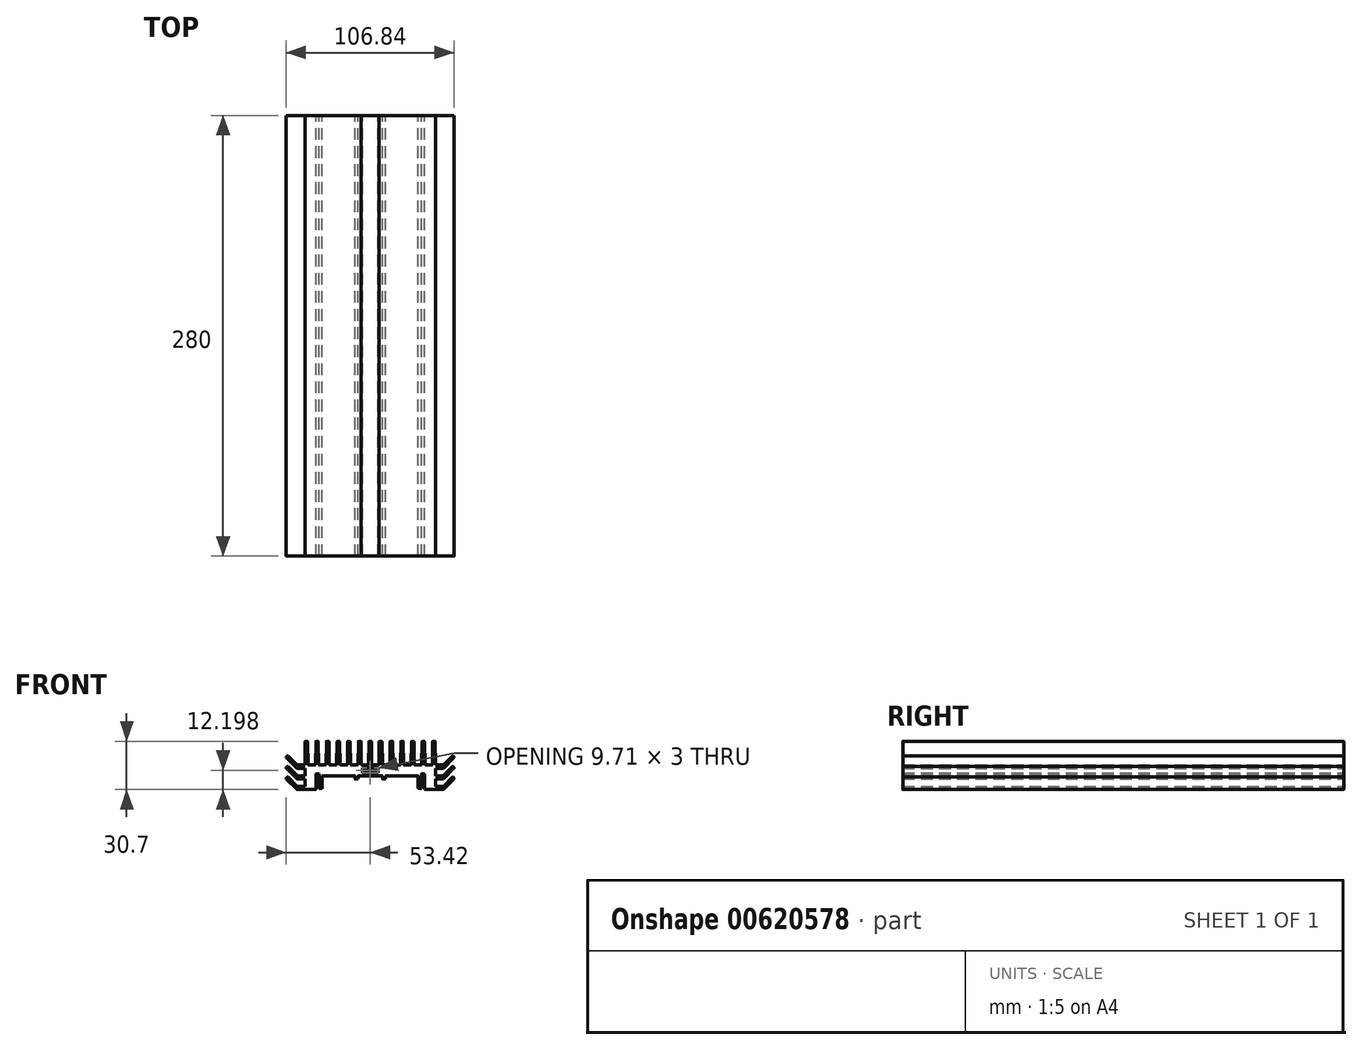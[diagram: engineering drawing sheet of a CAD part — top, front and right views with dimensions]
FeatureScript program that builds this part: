
annotation { "Feature Type Name" : "Feature", "Feature Type Description" : "" }
export const myFeature = defineFeature(function(context is Context, id is Id, definition is map)
    precondition{}
    {
        {
            var Q0;
            Q0=qCreatedBy(makeId("Front.planeOp"),FACE);
            var sketch = newSketch(context, id + "F0", { "sketchPlane" : qUnion([Q0])});
            skLineSegment(sketch, "E0", {"start": v(-32.5, -11.3) * mm, "end": v(-32.5, -2.4) * mm});
            skLineSegment(sketch, "E1", {"start": v(-32.7, -2.2) * mm, "end": v(-34.3, -2.2) * mm});
            skLineSegment(sketch, "E2", {"start": v(-34.5, -2.4) * mm, "end": v(-34.5, -12) * mm});
            skLineSegment(sketch, "E3", {"start": v(-39.75, 18.3) * mm, "end": v(-39.5, 3.7) * mm});
            skLineSegment(sketch, "E4", {"start": v(-9.75, -3.7) * mm, "end": v(-9.75, -5.3) * mm});
            skLineSegment(sketch, "E5", {"start": v(-9.55, -5.5) * mm, "end": v(-7.95, -5.5) * mm});
            skLineSegment(sketch, "E6", {"start": v(-39.3, 3.5) * mm, "end": v(-34.95, 3.5) * mm});
            skLineSegment(sketch, "E7", {"start": v(-41.5, 3.5) * mm, "end": v(-41.25, 18.3) * mm});
            skLineSegment(sketch, "E8", {"start": v(-41.05, 18.5) * mm, "end": v(-39.95, 18.5) * mm});
            skLineSegment(sketch, "E9", {"start": v(-41.5, 3.5) * mm, "end": v(-41.5, -12.2) * mm});
            skLineSegment(sketch, "E10.1.0.0", {"start": v(-33, 18.3) * mm, "end": v(-32.75, 3.7) * mm});
            skLineSegment(sketch, "E10.1.0.1", {"start": v(-32.55, 3.5) * mm, "end": v(-28.2, 3.5) * mm});
            skLineSegment(sketch, "E10.1.0.2", {"start": v(-34.75, 3.7) * mm, "end": v(-34.5, 18.3) * mm});
            skLineSegment(sketch, "E10.1.0.3", {"start": v(-34.3, 18.5) * mm, "end": v(-33.2, 18.5) * mm});
            skLineSegment(sketch, "E10.2.0.0", {"start": v(-26.25, 18.3) * mm, "end": v(-26, 3.7) * mm});
            skLineSegment(sketch, "E10.2.0.1", {"start": v(-25.8, 3.5) * mm, "end": v(-21.45, 3.5) * mm});
            skLineSegment(sketch, "E10.2.0.2", {"start": v(-28, 3.7) * mm, "end": v(-27.75, 18.3) * mm});
            skLineSegment(sketch, "E10.2.0.3", {"start": v(-27.55, 18.5) * mm, "end": v(-26.45, 18.5) * mm});
            skLineSegment(sketch, "E10.3.0.0", {"start": v(-19.5, 18.3) * mm, "end": v(-19.25, 3.7) * mm});
            skLineSegment(sketch, "E10.3.0.1", {"start": v(-19.05, 3.5) * mm, "end": v(-14.7, 3.5) * mm});
            skLineSegment(sketch, "E10.3.0.2", {"start": v(-21.25, 3.7) * mm, "end": v(-21, 18.3) * mm});
            skLineSegment(sketch, "E10.3.0.3", {"start": v(-20.8, 18.5) * mm, "end": v(-19.7, 18.5) * mm});
            skLineSegment(sketch, "E10.4.0.0", {"start": v(-12.75, 18.3) * mm, "end": v(-12.5, 3.7) * mm});
            skLineSegment(sketch, "E10.4.0.1", {"start": v(-12.3, 3.5) * mm, "end": v(-7.95, 3.5) * mm});
            skLineSegment(sketch, "E10.4.0.2", {"start": v(-14.5, 3.7) * mm, "end": v(-14.25, 18.3) * mm});
            skLineSegment(sketch, "E10.4.0.3", {"start": v(-14.05, 18.5) * mm, "end": v(-12.95, 18.5) * mm});
            skLineSegment(sketch, "E10.5.0.0", {"start": v(-5.75, 18.3) * mm, "end": v(-5.75, 3.7) * mm});
            skLineSegment(sketch, "E10.5.0.1", {"start": v(-5.55, 3.5) * mm, "end": v(-1.2, 3.5) * mm});
            skLineSegment(sketch, "E10.5.0.2", {"start": v(-7.75, 3.7) * mm, "end": v(-7.5, 18.3) * mm});
            skLineSegment(sketch, "E10.5.0.3", {"start": v(-7.3, 18.5) * mm, "end": v(-5.95, 18.5) * mm});
            skLineSegment(sketch, "E11.6.6.0", {"start": v(-1, 3.7) * mm, "end": v(-0.75, 18.3) * mm});
            skLineSegment(sketch, "E11.9.6.0", {"start": v(-0.55, 18.5) * mm, "end": v(0, 18.5) * mm});
            skPoint(sketch, "E12", {"position": v(0, 18.5) * mm});
            skLineSegment(sketch, "E13", {"start": v(0, 18.5) * mm, "end": v(0, 1.5) * mm});
            skLineSegment(sketch, "E14", {"start": v(-41.5, -12.2) * mm, "end": v(-34.7, -12.2) * mm});
            skLineSegment(sketch, "E15", {"start": v(-32.3, -11.5) * mm, "end": v(-30.7, -11.5) * mm});
            skLineSegment(sketch, "E16", {"start": v(-9.95, -3.5) * mm, "end": v(-30.32, -3.5) * mm});
            skLineSegment(sketch, "E17", {"start": v(-30.5, -11.3) * mm, "end": v(-30.52, -3.7) * mm});
            skLineSegment(sketch, "E18", {"start": v(-4.85, 1.3) * mm, "end": v(-4.85, -1.3) * mm});
            skLineSegment(sketch, "E19", {"start": v(0, -1.5) * mm, "end": v(0, -3.5) * mm});
            skLineSegment(sketch, "E20", {"start": v(-7.75, -3.7) * mm, "end": v(-7.75, -5.3) * mm});
            skPoint(sketch, "E21.visualSharp", {"position": v(-41.25, 18.5) * mm});
            skArc(sketch, "E21.filletArc", {"start": v(-41.05, 18.5) * mm, "mid": v(-41.2, 18.44) * mm, "end": v(-41.25, 18.3) * mm});
            skPoint(sketch, "E22.visualSharp", {"position": v(-39.75, 18.5) * mm});
            skArc(sketch, "E22.filletArc", {"start": v(-39.75, 18.3) * mm, "mid": v(-39.8, 18.44) * mm, "end": v(-39.95, 18.5) * mm});
            skPoint(sketch, "E23.visualSharp", {"position": v(-34.5, 18.5) * mm});
            skArc(sketch, "E23.filletArc", {"start": v(-34.3, 18.5) * mm, "mid": v(-34.44, 18.44) * mm, "end": v(-34.5, 18.3) * mm});
            skPoint(sketch, "E24.visualSharp", {"position": v(-33, 18.5) * mm});
            skArc(sketch, "E24.filletArc", {"start": v(-33, 18.3) * mm, "mid": v(-33.06, 18.44) * mm, "end": v(-33.2, 18.5) * mm});
            skPoint(sketch, "E25.visualSharp", {"position": v(-27.75, 18.5) * mm});
            skArc(sketch, "E25.filletArc", {"start": v(-27.55, 18.5) * mm, "mid": v(-27.7, 18.44) * mm, "end": v(-27.75, 18.3) * mm});
            skPoint(sketch, "E26.visualSharp", {"position": v(-26.25, 18.5) * mm});
            skArc(sketch, "E26.filletArc", {"start": v(-26.25, 18.3) * mm, "mid": v(-26.3, 18.44) * mm, "end": v(-26.45, 18.5) * mm});
            skPoint(sketch, "E27.visualSharp", {"position": v(-21, 18.5) * mm});
            skArc(sketch, "E27.filletArc", {"start": v(-20.8, 18.5) * mm, "mid": v(-20.94, 18.44) * mm, "end": v(-21, 18.3) * mm});
            skPoint(sketch, "E28.visualSharp", {"position": v(-19.5, 18.5) * mm});
            skArc(sketch, "E28.filletArc", {"start": v(-19.5, 18.3) * mm, "mid": v(-19.56, 18.44) * mm, "end": v(-19.7, 18.5) * mm});
            skPoint(sketch, "E29.visualSharp", {"position": v(-14.25, 18.5) * mm});
            skArc(sketch, "E29.filletArc", {"start": v(-14.05, 18.5) * mm, "mid": v(-14.2, 18.44) * mm, "end": v(-14.25, 18.3) * mm});
            skPoint(sketch, "E30.visualSharp", {"position": v(-12.75, 18.5) * mm});
            skArc(sketch, "E30.filletArc", {"start": v(-12.75, 18.3) * mm, "mid": v(-12.8, 18.44) * mm, "end": v(-12.95, 18.5) * mm});
            skPoint(sketch, "E31.visualSharp", {"position": v(-7.5, 18.5) * mm});
            skArc(sketch, "E31.filletArc", {"start": v(-7.3, 18.5) * mm, "mid": v(-7.44, 18.44) * mm, "end": v(-7.5, 18.3) * mm});
            skPoint(sketch, "E32.visualSharp", {"position": v(-5.75, 18.5) * mm});
            skArc(sketch, "E32.filletArc", {"start": v(-5.75, 18.3) * mm, "mid": v(-5.8, 18.44) * mm, "end": v(-5.95, 18.5) * mm});
            skPoint(sketch, "E33.visualSharp", {"position": v(-0.75, 18.5) * mm});
            skArc(sketch, "E33.filletArc", {"start": v(-0.55, 18.5) * mm, "mid": v(-0.7, 18.44) * mm, "end": v(-0.75, 18.3) * mm});
            skPoint(sketch, "E34.visualSharp", {"position": v(0, 1.5) * mm});
            skPoint(sketch, "E35.visualSharp", {"position": v(-4.85, 1.5) * mm});
            skArc(sketch, "E35.filletArc", {"start": v(-4.65, 1.5) * mm, "mid": v(-4.8, 1.44) * mm, "end": v(-4.85, 1.3) * mm});
            skPoint(sketch, "E36.visualSharp", {"position": v(-4.85, -1.5) * mm});
            skArc(sketch, "E36.filletArc", {"start": v(-4.85, -1.3) * mm, "mid": v(-4.8, -1.44) * mm, "end": v(-4.65, -1.5) * mm});
            skPoint(sketch, "E37.visualSharp", {"position": v(0, -1.5) * mm});
            skPoint(sketch, "E38.visualSharp", {"position": v(0, -3.5) * mm});
            skPoint(sketch, "E39.visualSharp", {"position": v(-7.75, -3.5) * mm});
            skArc(sketch, "E39.filletArc", {"start": v(-7.55, -3.5) * mm, "mid": v(-7.7, -3.56) * mm, "end": v(-7.75, -3.7) * mm});
            skPoint(sketch, "E40.visualSharp", {"position": v(-7.75, -5.5) * mm});
            skArc(sketch, "E40.filletArc", {"start": v(-7.95, -5.5) * mm, "mid": v(-7.8, -5.44) * mm, "end": v(-7.75, -5.3) * mm});
            skPoint(sketch, "E41.visualSharp", {"position": v(-9.75, -5.5) * mm});
            skArc(sketch, "E41.filletArc", {"start": v(-9.75, -5.3) * mm, "mid": v(-9.7, -5.44) * mm, "end": v(-9.55, -5.5) * mm});
            skPoint(sketch, "E42.visualSharp", {"position": v(-9.75, -3.5) * mm});
            skArc(sketch, "E42.filletArc", {"start": v(-9.75, -3.7) * mm, "mid": v(-9.8, -3.56) * mm, "end": v(-9.95, -3.5) * mm});
            skPoint(sketch, "E43.visualSharp", {"position": v(-30.52, -3.5) * mm});
            skArc(sketch, "E43.filletArc", {"start": v(-30.32, -3.5) * mm, "mid": v(-30.46, -3.56) * mm, "end": v(-30.52, -3.7) * mm});
            skPoint(sketch, "E44.visualSharp", {"position": v(-30.5, -11.5) * mm});
            skArc(sketch, "E44.filletArc", {"start": v(-30.7, -11.5) * mm, "mid": v(-30.56, -11.44) * mm, "end": v(-30.5, -11.3) * mm});
            skPoint(sketch, "E45.visualSharp", {"position": v(-32.5, -11.5) * mm});
            skArc(sketch, "E45.filletArc", {"start": v(-32.5, -11.3) * mm, "mid": v(-32.44, -11.44) * mm, "end": v(-32.3, -11.5) * mm});
            skPoint(sketch, "E46.visualSharp", {"position": v(-32.5, -2.2) * mm});
            skArc(sketch, "E46.filletArc", {"start": v(-32.5, -2.4) * mm, "mid": v(-32.56, -2.25) * mm, "end": v(-32.7, -2.2) * mm});
            skPoint(sketch, "E47.visualSharp", {"position": v(-34.5, -2.2) * mm});
            skArc(sketch, "E47.filletArc", {"start": v(-34.3, -2.2) * mm, "mid": v(-34.44, -2.25) * mm, "end": v(-34.5, -2.4) * mm});
            skPoint(sketch, "E48.visualSharp", {"position": v(-34.5, -12.2) * mm});
            skArc(sketch, "E48.filletArc", {"start": v(-34.7, -12.2) * mm, "mid": v(-34.56, -12.14) * mm, "end": v(-34.5, -12) * mm});
            skPoint(sketch, "E49.visualSharp", {"position": v(-41.5, -12.2) * mm});
            skPoint(sketch, "E50.visualSharp", {"position": v(-39.5, 3.5) * mm});
            skArc(sketch, "E50.filletArc", {"start": v(-39.5, 3.7) * mm, "mid": v(-39.44, 3.56) * mm, "end": v(-39.3, 3.5) * mm});
            skPoint(sketch, "E51.visualSharp", {"position": v(-34.75, 3.5) * mm});
            skArc(sketch, "E51.filletArc", {"start": v(-34.95, 3.5) * mm, "mid": v(-34.8, 3.56) * mm, "end": v(-34.75, 3.7) * mm});
            skPoint(sketch, "E52.visualSharp", {"position": v(-32.75, 3.5) * mm});
            skArc(sketch, "E52.filletArc", {"start": v(-32.75, 3.7) * mm, "mid": v(-32.7, 3.56) * mm, "end": v(-32.55, 3.5) * mm});
            skPoint(sketch, "E53.visualSharp", {"position": v(-28, 3.5) * mm});
            skArc(sketch, "E53.filletArc", {"start": v(-28.2, 3.5) * mm, "mid": v(-28.06, 3.56) * mm, "end": v(-28, 3.7) * mm});
            skPoint(sketch, "E54.visualSharp", {"position": v(-26, 3.5) * mm});
            skArc(sketch, "E54.filletArc", {"start": v(-26, 3.7) * mm, "mid": v(-25.94, 3.56) * mm, "end": v(-25.8, 3.5) * mm});
            skPoint(sketch, "E55.visualSharp", {"position": v(-21.25, 3.5) * mm});
            skArc(sketch, "E55.filletArc", {"start": v(-21.45, 3.5) * mm, "mid": v(-21.3, 3.56) * mm, "end": v(-21.25, 3.7) * mm});
            skPoint(sketch, "E56.visualSharp", {"position": v(-19.25, 3.5) * mm});
            skArc(sketch, "E56.filletArc", {"start": v(-19.25, 3.7) * mm, "mid": v(-19.2, 3.56) * mm, "end": v(-19.05, 3.5) * mm});
            skPoint(sketch, "E57.visualSharp", {"position": v(-14.5, 3.5) * mm});
            skArc(sketch, "E57.filletArc", {"start": v(-14.7, 3.5) * mm, "mid": v(-14.56, 3.56) * mm, "end": v(-14.5, 3.7) * mm});
            skPoint(sketch, "E58.visualSharp", {"position": v(-12.5, 3.5) * mm});
            skArc(sketch, "E58.filletArc", {"start": v(-12.5, 3.7) * mm, "mid": v(-12.44, 3.56) * mm, "end": v(-12.3, 3.5) * mm});
            skPoint(sketch, "E59.visualSharp", {"position": v(-7.75, 3.5) * mm});
            skArc(sketch, "E59.filletArc", {"start": v(-7.95, 3.5) * mm, "mid": v(-7.8, 3.56) * mm, "end": v(-7.75, 3.7) * mm});
            skPoint(sketch, "E60.visualSharp", {"position": v(-5.75, 3.5) * mm});
            skArc(sketch, "E60.filletArc", {"start": v(-5.75, 3.7) * mm, "mid": v(-5.7, 3.56) * mm, "end": v(-5.55, 3.5) * mm});
            skPoint(sketch, "E61.visualSharp", {"position": v(-1, 3.5) * mm});
            skArc(sketch, "E61.filletArc", {"start": v(-1.2, 3.5) * mm, "mid": v(-1.06, 3.56) * mm, "end": v(-1, 3.7) * mm});
            skLineSegment(sketch, "E62", {"start": v(-4.65, 1.5) * mm, "end": v(0, 1.5) * mm});
            skLineSegment(sketch, "E63", {"start": v(-4.65, -1.5) * mm, "end": v(0, -1.5) * mm});
            skLineSegment(sketch, "E64", {"start": v(-7.55, -3.5) * mm, "end": v(0, -3.5) * mm});
            skSolve(sketch);
        }
        {
            var Q0;
            Q0=qSketchRegion(id+"F0",true);
            extrude(context, id + "F1", {"entities" : qUnion([Q0]), "depth" : 280 * mm, "offsetDistance" : 25 * mm});
        }
        {
            var Q0;
            Q0=qCreatedBy(makeId("Front.planeOp"),FACE);
            var sketch = newSketch(context, id + "F2", { "sketchPlane" : qUnion([Q0])});
            skLineSegment(sketch, "E65", {"start": v(-41.5, -12.2) * mm, "end": v(-46.5, -12.2) * mm});
            skLineSegment(sketch, "E66", {"start": v(-46.56, -12.14) * mm, "end": v(-53.36, -5.34) * mm});
            skLineSegment(sketch, "E67", {"start": v(-53.36, -5.05) * mm, "end": v(-52.58, -4.28) * mm});
            skLineSegment(sketch, "E68", {"start": v(-52.3, -4.28) * mm, "end": v(-46.44, -10.14) * mm});
            skLineSegment(sketch, "E69", {"start": v(-46.3, -10.2) * mm, "end": v(-41.5, -10.2) * mm});
            skLineSegment(sketch, "E70", {"start": v(-41.5, -12.2) * mm, "end": v(-41.5, -10.2) * mm});
            skLineSegment(sketch, "E71.0.1.0", {"start": v(-46.56, -5.39) * mm, "end": v(-53.36, 1.41) * mm});
            skLineSegment(sketch, "E71.0.1.1", {"start": v(-41.5, -5.44) * mm, "end": v(-46.42, -5.44) * mm});
            skLineSegment(sketch, "E71.0.1.2", {"start": v(-46.3, -3.44) * mm, "end": v(-41.5, -3.44) * mm});
            skLineSegment(sketch, "E71.0.1.3", {"start": v(-41.5, -5.44) * mm, "end": v(-41.5, -3.44) * mm});
            skLineSegment(sketch, "E71.0.1.4", {"start": v(-52.3, 2.47) * mm, "end": v(-46.44, -3.39) * mm});
            skLineSegment(sketch, "E71.0.1.5", {"start": v(-53.36, 1.7) * mm, "end": v(-52.58, 2.47) * mm});
            skLineSegment(sketch, "E71.0.2.0", {"start": v(-46.56, 1.36) * mm, "end": v(-53.36, 8.16) * mm});
            skLineSegment(sketch, "E71.0.2.1", {"start": v(-41.5, 1.3) * mm, "end": v(-46.42, 1.3) * mm});
            skLineSegment(sketch, "E71.0.2.2", {"start": v(-46.3, 3.3) * mm, "end": v(-41.5, 3.3) * mm});
            skLineSegment(sketch, "E71.0.2.3", {"start": v(-41.5, 1.3) * mm, "end": v(-41.5, 3.3) * mm});
            skLineSegment(sketch, "E71.0.2.4", {"start": v(-52.3, 9.22) * mm, "end": v(-46.44, 3.36) * mm});
            skLineSegment(sketch, "E71.0.2.5", {"start": v(-53.36, 8.45) * mm, "end": v(-52.58, 9.22) * mm});
            skLineSegment(sketch, "E71.direction1", {"start": v(-46.42, -12.2) * mm, "end": v(-22.16, -12.2) * mm, "construction": true});
            skLineSegment(sketch, "E71.direction2", {"start": v(-46.5, -12.2) * mm, "end": v(-46.5, -5.44) * mm, "construction": true});
            skPoint(sketch, "E72.visualSharp", {"position": v(-52.44, 9.37) * mm});
            skArc(sketch, "E72.filletArc", {"start": v(-52.3, 9.22) * mm, "mid": v(-52.44, 9.28) * mm, "end": v(-52.58, 9.22) * mm});
            skPoint(sketch, "E73.visualSharp", {"position": v(-53.5, 8.3) * mm});
            skArc(sketch, "E73.filletArc", {"start": v(-53.36, 8.45) * mm, "mid": v(-53.42, 8.3) * mm, "end": v(-53.36, 8.16) * mm});
            skPoint(sketch, "E74.visualSharp", {"position": v(-46.38, 3.3) * mm});
            skArc(sketch, "E74.filletArc", {"start": v(-46.44, 3.36) * mm, "mid": v(-46.37, 3.32) * mm, "end": v(-46.3, 3.3) * mm});
            skPoint(sketch, "E75.visualSharp", {"position": v(-46.5, 1.3) * mm});
            skArc(sketch, "E75.filletArc", {"start": v(-46.56, 1.36) * mm, "mid": v(-46.5, 1.32) * mm, "end": v(-46.42, 1.3) * mm});
            skPoint(sketch, "E76.visualSharp", {"position": v(-46.38, -3.44) * mm});
            skArc(sketch, "E76.filletArc", {"start": v(-46.44, -3.39) * mm, "mid": v(-46.37, -3.43) * mm, "end": v(-46.3, -3.44) * mm});
            skPoint(sketch, "E77.visualSharp", {"position": v(-53.5, 1.56) * mm});
            skArc(sketch, "E77.filletArc", {"start": v(-53.36, 1.7) * mm, "mid": v(-53.42, 1.56) * mm, "end": v(-53.36, 1.41) * mm});
            skPoint(sketch, "E78.visualSharp", {"position": v(-52.44, 2.62) * mm});
            skArc(sketch, "E78.filletArc", {"start": v(-52.3, 2.47) * mm, "mid": v(-52.44, 2.53) * mm, "end": v(-52.58, 2.47) * mm});
            skPoint(sketch, "E79.visualSharp", {"position": v(-46.5, -5.44) * mm});
            skArc(sketch, "E79.filletArc", {"start": v(-46.56, -5.39) * mm, "mid": v(-46.5, -5.43) * mm, "end": v(-46.42, -5.44) * mm});
            skPoint(sketch, "E80.visualSharp", {"position": v(-46.38, -10.2) * mm});
            skArc(sketch, "E80.filletArc", {"start": v(-46.44, -10.14) * mm, "mid": v(-46.37, -10.18) * mm, "end": v(-46.3, -10.2) * mm});
            skPoint(sketch, "E81.visualSharp", {"position": v(-46.5, -12.2) * mm});
            skArc(sketch, "E81.filletArc", {"start": v(-46.56, -12.14) * mm, "mid": v(-46.5, -12.18) * mm, "end": v(-46.42, -12.2) * mm});
            skPoint(sketch, "E82.visualSharp", {"position": v(-52.44, -4.13) * mm});
            skArc(sketch, "E82.filletArc", {"start": v(-52.3, -4.28) * mm, "mid": v(-52.44, -4.22) * mm, "end": v(-52.58, -4.28) * mm});
            skPoint(sketch, "E83.visualSharp", {"position": v(-53.5, -5.2) * mm});
            skArc(sketch, "E83.filletArc", {"start": v(-53.36, -5.05) * mm, "mid": v(-53.42, -5.2) * mm, "end": v(-53.36, -5.34) * mm});
            skSolve(sketch);
        }
        {
            var Q0;
            Q0=qSketchRegion(id+"F2",true);
            extrude(context, id + "F3", {"entities" : qUnion([Q0]), "operationType" : NewBodyOperationType.ADD, "depth" : 280 * mm, "offsetDistance" : 25 * mm});
        }
        {
            var Q0;
            Q0=makeQuery(id+"F1.opExtrude","SWEPT_BODY",BODY,{"disambiguationData":[OSD([sQuery(id+"F0.wireOp",EDGE,"QOM90pkH-KK3E-2t4G-PR0d-VXwYNY4fjtTb"),sQuery(id+"F0.wireOp",EDGE,"Wt8m1K6G-Pg8W-yz88-BKp3-o8GU5yjb4NPO"),sQuery(id+"F0.wireOp",EDGE,"F3vcOgBq-LlWr-xvjw-e04Y-niSAJOFfG4p2"),sQuery(id+"F0.wireOp",EDGE,"u1mY0JJN-f7Kk-nBfH-W6HL-n9qIg2MDpbPP"),sQuery(id+"F0.wireOp",EDGE,"E0"),sQuery(id+"F0.wireOp",EDGE,"E1"),sQuery(id+"F0.wireOp",EDGE,"E2"),sQuery(id+"F0.wireOp",EDGE,"WuwbFeWC-LNyf-1R1Z-RHmS-f9KyMF8TMt9i"),sQuery(id+"F0.wireOp",EDGE,"UM4JaTJU-Vk1M-XgEN-ImDx-eCgJd49Y6FMu"),sQuery(id+"F0.wireOp",EDGE,"OvlMNyBG-IFKC-w7DX-ZWVS-3YzXS4CVPNQT"),sQuery(id+"F0.wireOp",EDGE,"jmIuwl2N-ih4h-DjTB-hYCO-kHODNnBOpXJs"),sQuery(id+"F0.wireOp",EDGE,"E3"),sQuery(id+"F0.wireOp",EDGE,"E4"),sQuery(id+"F0.wireOp",EDGE,"E5"),sQuery(id+"F0.wireOp",EDGE,"DATJw4Rr-6OHI-e9sL-mig8-pdpoUj6XXJZJ"),sQuery(id+"F0.wireOp",EDGE,"ed90f767-a289-48e3-8617-8c3c22fb4d72.trimOffspring"),sQuery(id+"F0.wireOp",EDGE,"E6"),sQuery(id+"F0.wireOp",EDGE,"E7"),sQuery(id+"F0.wireOp",EDGE,"E8"),sQuery(id+"F0.wireOp",EDGE,"E9"),sQuery(id+"F0.wireOp",EDGE,"E10.1.0.0"),sQuery(id+"F0.wireOp",EDGE,"E10.1.0.1"),sQuery(id+"F0.wireOp",EDGE,"E10.1.0.2"),sQuery(id+"F0.wireOp",EDGE,"E10.1.0.3"),sQuery(id+"F0.wireOp",EDGE,"E10.2.0.0"),sQuery(id+"F0.wireOp",EDGE,"E10.2.0.1"),sQuery(id+"F0.wireOp",EDGE,"E10.2.0.2"),sQuery(id+"F0.wireOp",EDGE,"E10.2.0.3"),sQuery(id+"F0.wireOp",EDGE,"E10.3.0.0"),sQuery(id+"F0.wireOp",EDGE,"E10.3.0.1"),sQuery(id+"F0.wireOp",EDGE,"E10.3.0.2"),sQuery(id+"F0.wireOp",EDGE,"E10.3.0.3"),sQuery(id+"F0.wireOp",EDGE,"E10.4.0.0"),sQuery(id+"F0.wireOp",EDGE,"E10.4.0.1"),sQuery(id+"F0.wireOp",EDGE,"E10.4.0.2"),sQuery(id+"F0.wireOp",EDGE,"E10.4.0.3"),sQuery(id+"F0.wireOp",EDGE,"E10.5.0.0"),sQuery(id+"F0.wireOp",EDGE,"E10.5.0.1"),sQuery(id+"F0.wireOp",EDGE,"E10.5.0.2"),sQuery(id+"F0.wireOp",EDGE,"E10.5.0.3"),sQuery(id+"F0.wireOp",EDGE,"E11.6.6.0"),sQuery(id+"F0.wireOp",EDGE,"E11.9.6.0"),sQuery(id+"F0.wireOp",EDGE,"yGFb3Jfo-Lhlh-xzfz-Ljs9-34xcXF1H7Gp1"),sQuery(id+"F0.wireOp",EDGE,"dxc8wIRG-n3ac-7oqY-UQSt-FR4flQWY79jH"),sQuery(id+"F0.wireOp",EDGE,"pMfyub31-Xo22-kmQh-hgcO-EaUa3d53Z9ym"),sQuery(id+"F0.wireOp",EDGE,"EXS0VTzR-uZRH-gpkk-ciJv-APifiNII5ex7"),sQuery(id+"F0.wireOp",EDGE,"j9COY3aO-4lFf-zBAU-mgS4-eOpnypJtWWPn")])]});
            var Q1;
            Q1=makeQuery(id+"F1.opExtrude","SWEPT_FACE",FACE,{"disambiguationData":[OSD([sQuery(id+"F0.wireOp",EDGE,"E13")])]});
            mirror(context, id + "F4", {"operationType" : NewBodyOperationType.ADD, "entities" : qUnion([Q0]), "mirrorPlane" : qUnion([Q1])});
        }
    });
